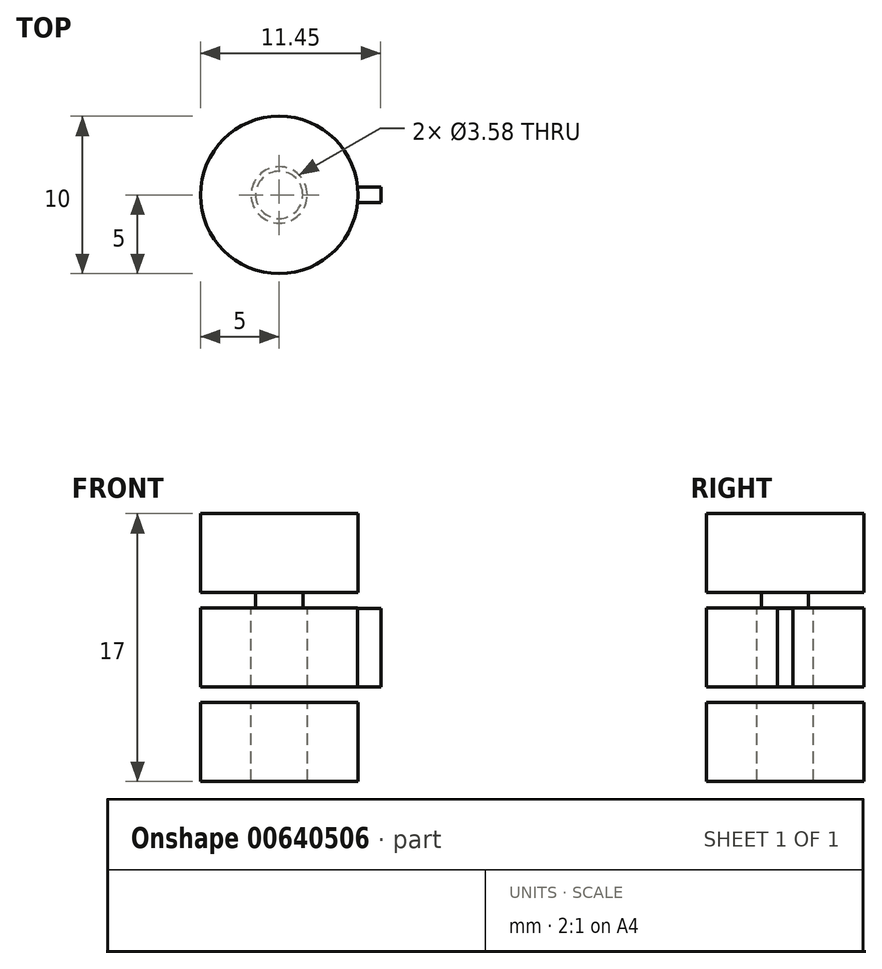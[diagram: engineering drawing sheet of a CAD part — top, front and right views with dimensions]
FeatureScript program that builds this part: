
annotation { "Feature Type Name" : "Feature", "Feature Type Description" : "" }
export const myFeature = defineFeature(function(context is Context, id is Id, definition is map)
    precondition{}
    {
        {
            var Q0;
            Q0=qCreatedBy(makeId("Top.planeOp"),FACE);
            var sketch = newSketch(context, id + "F0", { "sketchPlane" : qUnion([Q0])});
            skCircle(sketch, "E0", {"center": v(0, 0) * mm, "radius": 5 * mm});
            skSolve(sketch);
        }
        {
            var Q0;
            Q0 = qSketchRegion(id + "F0", true);
            extrude(context, id + "F1", {"entities" : qUnion([Q0]), "depth" : 5 * mm, "offsetDistance" : 25 * mm});
        }
        {
            var Q0;
            Q0=makeQuery(id+"F1.opExtrude","CAP_FACE",FACE,{"disambiguationData":[OSD([sQuery(id+"F0.wireOp",EDGE,"E0")])],"isStart":false});
            var sketch = newSketch(context, id + "F2", { "sketchPlane" : qUnion([Q0])});
            skCircle(sketch, "E1", {"center": v(0, 0) * mm, "radius": 1.5 * mm});
            skSolve(sketch);
        }
        {
            var Q0;
            Q0 = qSketchRegion(id + "F2", true);
            extrude(context, id + "F3", {"entities" : qUnion([Q0]), "operationType" : NewBodyOperationType.ADD, "depth" : 7 * mm, "offsetDistance" : 25 * mm});
        }
        {
            var Q0;
            Q0=makeQuery(id+"F1.opExtrude","CAP_FACE",FACE,{"disambiguationData":[OSD([sQuery(id+"F0.wireOp",EDGE,"E0")])],"isStart":false});
            var sketch = newSketch(context, id + "F4", { "sketchPlane" : qUnion([Q0])});
            skCircle(sketch, "E2", {"center": v(0, 0) * mm, "radius": 5 * mm});
            skSolve(sketch);
        }
        {
            var Q0;
            Q0 = qSketchRegion(id + "F4", true);
            extrude(context, id + "F5", {"entities" : qUnion([Q0]), "depth" : 5 * mm, "offsetDistance" : 25 * mm});
        }
        {
            var Q0;
            Q0=makeQuery(id+"F5.opExtrude","SWEPT_BODY",BODY,{"disambiguationData":[OSD([sQuery(id+"F4.wireOp",EDGE,"E2")])]});
            transform(context, id + "F6", {"entities" : qUnion([Q0]), "transformType" : TransformType.TRANSLATION_3D, "dx" : 0 * mm, "dy" : 0 * mm, "dz" : 1 * mm, "makeCopy" : false});
        }
        {
            var Q0;
            Q0=makeQuery(id+"F5.opExtrude","CAP_FACE",FACE,{"disambiguationData":[OSD([sQuery(id+"F4.wireOp",EDGE,"E2")])],"isStart":false});
            var sketch = newSketch(context, id + "F7", { "sketchPlane" : qUnion([Q0])});
            skCircle(sketch, "E3", {"center": v(0, 0) * mm, "radius": 1.79 * mm});
            skSolve(sketch);
        }
        {
            var Q0;
            Q0 = qSketchRegion(id + "F7", true);
            extrude(context, id + "F8", {"entities" : qUnion([Q0]), "operationType" : NewBodyOperationType.REMOVE, "oppositeDirection" : true, "depth" : 25 * mm, "offsetDistance" : 25 * mm});
        }
        {
            var Q0;
            Q0=makeQuery(id+"F3.opExtrude","CAP_FACE",FACE,{"disambiguationData":[OSD([sQuery(id+"F2.wireOp",EDGE,"E1")])],"isStart":false});
            var sketch = newSketch(context, id + "F9", { "sketchPlane" : qUnion([Q0])});
            skCircle(sketch, "E4", {"center": v(0, 0) * mm, "radius": 5 * mm});
            skSolve(sketch);
        }
        {
            var Q0;
            Q0 = qSketchRegion(id + "F9", true);
            extrude(context, id + "F10", {"entities" : qUnion([Q0]), "operationType" : NewBodyOperationType.ADD, "depth" : 5 * mm, "offsetDistance" : 25 * mm});
        }
        {
            var Q0;
            Q0=qCreatedBy(makeId("Front.planeOp"),FACE);
            var sketch = newSketch(context, id + "F11", { "sketchPlane" : qUnion([Q0])});
            skLineSegment(sketch, "E5.bottom", {"start": v(4.9, 11) * mm, "end": v(6.45, 11) * mm});
            skLineSegment(sketch, "E5.top", {"start": v(4.9, 6) * mm, "end": v(6.45, 6) * mm});
            skLineSegment(sketch, "E5.left", {"start": v(4.9, 11) * mm, "end": v(4.9, 6) * mm});
            skLineSegment(sketch, "E5.right", {"start": v(6.45, 11) * mm, "end": v(6.45, 6) * mm});
            skSolve(sketch);
        }
        {
            var Q0;
            Q0 = qSketchRegion(id + "F11", true);
            extrude(context, id + "F12", {"entities" : qUnion([Q0]), "operationType" : NewBodyOperationType.ADD, "depth" : .5 * mm, "offsetDistance" : 25 * mm, "hasSecondDirection" : true, "secondDirectionOppositeDirection" : true, "secondDirectionDepth" : .5 * mm});
        }
    });
